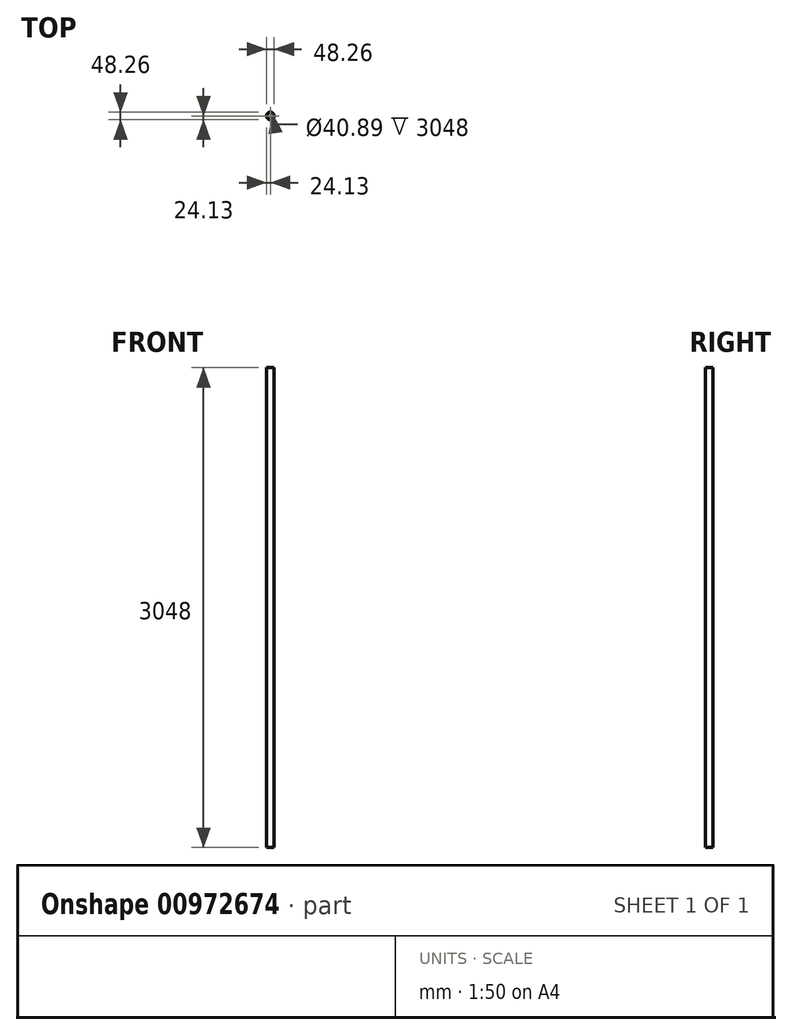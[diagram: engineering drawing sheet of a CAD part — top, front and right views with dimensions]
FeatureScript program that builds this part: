
annotation { "Feature Type Name" : "Feature", "Feature Type Description" : "" }
export const myFeature = defineFeature(function(context is Context, id is Id, definition is map)
    precondition{}
    {
        {
            var Q0;
            Q0=qCreatedBy(makeId("Top.planeOp"),FACE);
            var sketch = newSketch(context, id + "F0", { "sketchPlane" : qUnion([Q0])});
            skCircle(sketch, "E0", {"center": v(0, 0) * mm, "radius": 24.13 * mm});
            skCircle(sketch, "E1", {"center": v(0, 0) * mm, "radius": 20.45 * mm});
            skSolve(sketch);
        }
        {
            var Q0;
            Q0 = qSketchRegion(id + "F0", true);
            extrude(context, id + "F1", {"entities" : qUnion([Q0]), "depth" : 3048 * mm, "offsetDistance" : 25.4 * mm});
        }
    });
